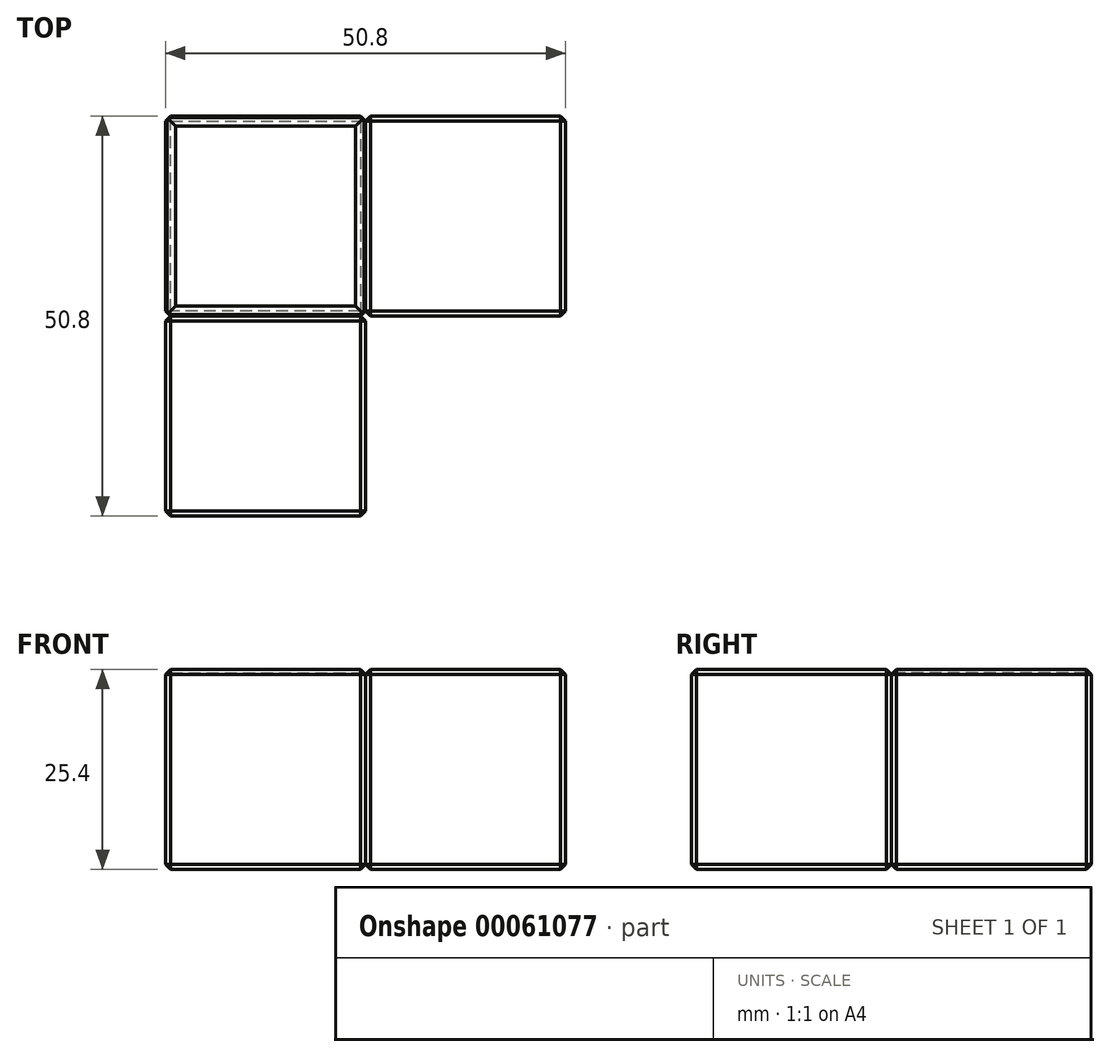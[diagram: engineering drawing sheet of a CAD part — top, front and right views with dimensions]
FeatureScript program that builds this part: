
annotation { "Feature Type Name" : "Feature", "Feature Type Description" : "" }
export const myFeature = defineFeature(function(context is Context, id is Id, definition is map)
    precondition{}
    {
        {
            var Q0;
            Q0=qCreatedBy(makeId("Top.planeOp"),FACE);
            var sketch = newSketch(context, id + "F0", { "sketchPlane" : qUnion([Q0])});
            skLineSegment(sketch, "E0.bottom", {"start": v(0, 0) * mm, "end": v(-25.4, 0) * mm});
            skLineSegment(sketch, "E0.top", {"start": v(0, 25.4) * mm, "end": v(-25.4, 25.4) * mm});
            skLineSegment(sketch, "E0.left", {"start": v(0, 0) * mm, "end": v(0, 25.4) * mm});
            skLineSegment(sketch, "E0.right", {"start": v(-25.4, 0) * mm, "end": v(-25.4, 25.4) * mm});
            skLineSegment(sketch, "E1.bottom", {"start": v(0, 0) * mm, "end": v(25.4, 0) * mm});
            skLineSegment(sketch, "E1.top", {"start": v(0, 25.4) * mm, "end": v(25.4, 25.4) * mm});
            skLineSegment(sketch, "E1.right", {"start": v(25.4, 0) * mm, "end": v(25.4, 25.4) * mm});
            skLineSegment(sketch, "E2.top", {"start": v(0, -25.4) * mm, "end": v(-25.4, -25.4) * mm});
            skLineSegment(sketch, "E2.left", {"start": v(0, 0) * mm, "end": v(0, -25.4) * mm});
            skLineSegment(sketch, "E2.right", {"start": v(-25.4, 0) * mm, "end": v(-25.4, -25.4) * mm});
            skSolve(sketch);
        }
        {
            var Q0;
            Q0=makeQuery(id+"F0.imprint","IMPRINT",FACE,{"disambiguationData":[TD([[makeQuery(id+"F0.imprint","IMPRINT",EDGE,{"derivedFrom":sQuery(id+"F0.wireOp",EDGE,"E0.top")}),1.0]])]});
            extrude(context, id + "F1", {"entities" : qUnion([Q0]), "depth" : 25.4 * mm});
        }
        {
            var Q0;
            Q0=makeQuery(id+"F1.opExtrude","CAP_FACE",FACE,{"disambiguationData":[OSD([sQuery(id+"F0.wireOp",EDGE,"E0.top"),sQuery(id+"F0.wireOp",EDGE,"E0.right"),sQuery(id+"F0.wireOp",EDGE,"E1.bottom"),sQuery(id+"F0.wireOp",EDGE,"E1.top"),sQuery(id+"F0.wireOp",EDGE,"E1.right"),sQuery(id+"F0.wireOp",EDGE,"E2.top"),sQuery(id+"F0.wireOp",EDGE,"E2.left"),sQuery(id+"F0.wireOp",EDGE,"E2.right")])],"isStart":true});
            var Q1;
            Q1=makeQuery(id+"F1.opExtrude","CAP_FACE",FACE,{"disambiguationData":[OSD([sQuery(id+"F0.wireOp",EDGE,"E0.top"),sQuery(id+"F0.wireOp",EDGE,"E0.right"),sQuery(id+"F0.wireOp",EDGE,"E1.bottom"),sQuery(id+"F0.wireOp",EDGE,"E1.top"),sQuery(id+"F0.wireOp",EDGE,"E1.right"),sQuery(id+"F0.wireOp",EDGE,"E2.top"),sQuery(id+"F0.wireOp",EDGE,"E2.left"),sQuery(id+"F0.wireOp",EDGE,"E2.right")])],"isStart":false});
            var Q2;
            Q2=makeQuery(id+"F1.opExtrude","SWEPT_EDGE",EDGE,{"disambiguationData":[OSD([sQuery(id+"F0.wireOp",EDGE,"E1.top"),sQuery(id+"F0.wireOp",EDGE,"E1.right")])]});
            var Q3;
            Q3=makeQuery(id+"F1.opExtrude","SWEPT_EDGE",EDGE,{"disambiguationData":[OSD([sQuery(id+"F0.wireOp",EDGE,"E1.bottom"),sQuery(id+"F0.wireOp",EDGE,"E1.right")])]});
            var Q4;
            Q4=makeQuery(id+"F1.opExtrude","SWEPT_FACE",FACE,{"disambiguationData":[OSD([sQuery(id+"F0.wireOp",EDGE,"E0.right"),sQuery(id+"F0.wireOp",EDGE,"E2.right")])]});
            chamfer(context, id + "F2", {"entities" : qUnion([Q0, Q1, Q2, Q3, Q4]), "width" : 0.64 * mm, "tangentPropagation" : true});
        }
        {
            var Q0;
            Q0=makeQuery(id+"F0.imprint","IMPRINT",FACE,{"disambiguationData":[TD([[makeQuery(id+"F0.imprint","IMPRINT",EDGE,{"derivedFrom":sQuery(id+"F0.wireOp",EDGE,"E0.bottom")}),1.0]])]});
            extrude(context, id + "F3", {"entities" : qUnion([Q0]), "depth" : 25.4 * mm});
        }
        {
            var Q0;
            Q0=makeQuery(id+"F0.imprint","IMPRINT",FACE,{"disambiguationData":[TD([[makeQuery(id+"F0.imprint","IMPRINT",EDGE,{"derivedFrom":sQuery(id+"F0.wireOp",EDGE,"E1.bottom")}),1.0]])]});
            extrude(context, id + "F4", {"entities" : qUnion([Q0]), "depth" : 25.4 * mm});
        }
        {
            var Q0;
            Q0=makeQuery(id+"F3.opExtrude","CAP_FACE",FACE,{"disambiguationData":[OSD([sQuery(id+"F0.wireOp",EDGE,"E0.bottom"),sQuery(id+"F0.wireOp",EDGE,"E2.top"),sQuery(id+"F0.wireOp",EDGE,"E2.left"),sQuery(id+"F0.wireOp",EDGE,"E2.right")])],"isStart":true});
            var Q1;
            Q1=makeQuery(id+"F3.opExtrude","SWEPT_FACE",FACE,{"disambiguationData":[OSD([sQuery(id+"F0.wireOp",EDGE,"E2.right")])]});
            var Q2;
            Q2=makeQuery(id+"F3.opExtrude","SWEPT_FACE",FACE,{"disambiguationData":[OSD([sQuery(id+"F0.wireOp",EDGE,"E2.top")])]});
            var Q3;
            Q3=makeQuery(id+"F3.opExtrude","SWEPT_FACE",FACE,{"disambiguationData":[OSD([sQuery(id+"F0.wireOp",EDGE,"E2.left")])]});
            var Q4;
            Q4=makeQuery(id+"F3.opExtrude","CAP_FACE",FACE,{"disambiguationData":[OSD([sQuery(id+"F0.wireOp",EDGE,"E0.bottom"),sQuery(id+"F0.wireOp",EDGE,"E2.top"),sQuery(id+"F0.wireOp",EDGE,"E2.left"),sQuery(id+"F0.wireOp",EDGE,"E2.right")])],"isStart":false});
            var Q5;
            Q5=makeQuery(id+"F4.opExtrude","CAP_FACE",FACE,{"disambiguationData":[OSD([sQuery(id+"F0.wireOp",EDGE,"E1.bottom"),sQuery(id+"F0.wireOp",EDGE,"E1.top"),sQuery(id+"F0.wireOp",EDGE,"E0.left"),sQuery(id+"F0.wireOp",EDGE,"E1.right")])],"isStart":false});
            var Q6;
            Q6=makeQuery(id+"F4.opExtrude","SWEPT_FACE",FACE,{"disambiguationData":[OSD([sQuery(id+"F0.wireOp",EDGE,"E1.bottom")])]});
            var Q7;
            Q7=makeQuery(id+"F4.opExtrude","CAP_FACE",FACE,{"disambiguationData":[OSD([sQuery(id+"F0.wireOp",EDGE,"E1.bottom"),sQuery(id+"F0.wireOp",EDGE,"E1.top"),sQuery(id+"F0.wireOp",EDGE,"E0.left"),sQuery(id+"F0.wireOp",EDGE,"E1.right")])],"isStart":true});
            var Q8;
            Q8=makeQuery(id+"F4.opExtrude","SWEPT_FACE",FACE,{"disambiguationData":[OSD([sQuery(id+"F0.wireOp",EDGE,"E1.right")])]});
            var Q9;
            Q9=makeQuery(id+"F4.opExtrude","SWEPT_FACE",FACE,{"disambiguationData":[OSD([sQuery(id+"F0.wireOp",EDGE,"E1.top")])]});
            var Q10;
            Q10=makeQuery(id+"F1.opExtrude","CAP_FACE",FACE,{"disambiguationData":[OSD([sQuery(id+"F0.wireOp",EDGE,"E0.top"),sQuery(id+"F0.wireOp",EDGE,"E0.right"),sQuery(id+"F0.wireOp",EDGE,"E0.left"),sQuery(id+"F0.wireOp",EDGE,"E0.bottom")])],"isStart":false});
            chamfer(context, id + "F5", {"entities" : qUnion([Q0, Q1, Q2, Q3, Q4, Q5, Q6, Q7, Q8, Q9, Q10]), "width" : 0.64 * mm, "tangentPropagation" : true});
        }
    });
